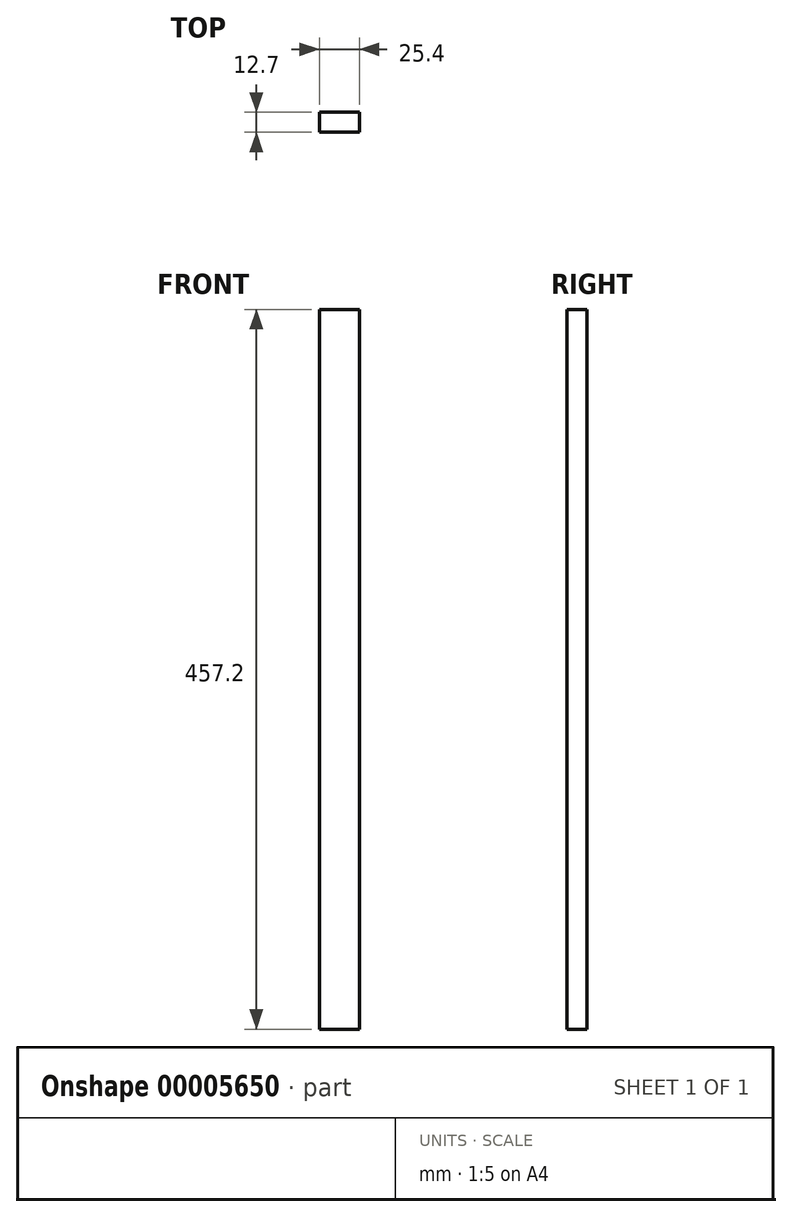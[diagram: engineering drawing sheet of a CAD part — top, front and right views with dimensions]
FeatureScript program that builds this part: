
annotation { "Feature Type Name" : "Feature", "Feature Type Description" : "" }
export const myFeature = defineFeature(function(context is Context, id is Id, definition is map)
    precondition{}
    {
        {
            var Q0;
            Q0=qCreatedBy(makeId("Front.planeOp"),FACE);
            var sketch = newSketch(context, id + "F0", { "sketchPlane" : qUnion([Q0])});
            skLineSegment(sketch, "E0.bottom", {"start": v(0, 0) * mm, "end": v(25.4, 0) * mm});
            skLineSegment(sketch, "E0.top", {"start": v(0, 457.2) * mm, "end": v(25.4, 457.2) * mm});
            skLineSegment(sketch, "E0.left", {"start": v(0, 0) * mm, "end": v(0, 457.2) * mm});
            skLineSegment(sketch, "E0.right", {"start": v(25.4, 0) * mm, "end": v(25.4, 457.2) * mm});
            skSolve(sketch);
        }
        {
            var Q0;
            Q0 = qSketchRegion(id + "F0", true);
            extrude(context, id + "F1", {"entities" : qUnion([Q0]), "depth" : 12.7 * mm});
        }
        {
            var Q0;
            Q0=makeQuery(id+"F1.opExtrude","SWEPT_FACE",FACE,{"disambiguationData":[OSD([sQuery(id+"F0.wireOp",EDGE,"E0.right")])]});
            var sketch = newSketch(context, id + "F2", { "sketchPlane" : qUnion([Q0])});
            skLineSegment(sketch, "E1.bottom", {"start": v(-3.18, 457.2) * mm, "end": v(-9.53, 457.2) * mm});
            skLineSegment(sketch, "E1.top", {"start": v(-3.17, 0) * mm, "end": v(-9.52, 0) * mm});
            skLineSegment(sketch, "E1.left", {"start": v(-3.18, 457.2) * mm, "end": v(-3.17, 0) * mm});
            skLineSegment(sketch, "E1.right", {"start": v(-9.53, 457.2) * mm, "end": v(-9.52, 0) * mm});
            skSolve(sketch);
        }
        {
            var Q0;
            Q0 = qSketchRegion(id + "F2", true);
            extrude(context, id + "F3", {"entities" : qUnion([Q0]), "depth" : 3.17 * mm});
        }
        {
            var Q0;
            Q0=makeQuery(id+"F3.opExtrude","SWEPT_BODY",BODY,{"disambiguationData":[OSD([sQuery(id+"F2.wireOp",EDGE,"E1.bottom"),sQuery(id+"F2.wireOp",EDGE,"E1.top"),sQuery(id+"F2.wireOp",EDGE,"E1.left"),sQuery(id+"F2.wireOp",EDGE,"E1.right")])]});
            deleteBodies(context, id + "F4", {"entities" : qUnion([Q0])});
        }
    });
